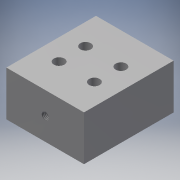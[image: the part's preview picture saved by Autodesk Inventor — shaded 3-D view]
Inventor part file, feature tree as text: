
AUTODESK INVENTOR PART (.ipt)
format: ipt  version: 2016 (Build 200138000, 138)  size: 133,120 bytes
history: native  units: mm (DEFAULTED — no unit token found)
features: sketch x4, extrude x2, hole x2, mirror x1
ambient origin geometry x8: Origin, YZ Plane, XZ Plane, XY Plane, X Axis, Y Axis, Z Axis, Center Point
bodies: Solid1 (feature_tree)
feature tree (9):
  extrude  "Extrusion1"  Depth=44.0mm
  hole  "Hole1"  [1 undecoded]
  mirror  "Mirror1"
  extrude  "Extrusion2"  [1 undecoded]
  sketch  "Sketch2"  dims[d0=50.8mm d1=44.0mm]
  sketch  "Sketch3"  dims[d2=25.4mm d3=0.0mm]
  hole  "Hole2"  [1 undecoded]
  sketch  "Sketch5"  dims[d11=6.0mm d12=6.0mm d13=6.0mm d14=6.0mm d15=20.0mm d16=15.0mm d18=0.0mm d19=5.0mm d20=6.0mm d21=20.594885mm d22=90.0deg d23=2.0mm d24=4.0mm d25=8.0mm d26=3.5mm]
  sketch  "Sketch4"  dims[d4=4.134mm d5=10.0mm d6=4.0mm d7=2.0mm d8=90.0deg d9=19.05mm d10=20.594885mm]
note: 3 required parameter values undecoded (feature->parameter linkage not recoverable at this tier; creation-order binding heuristic only, values carry confidence <= 0.55)
